# Revit family: Haworth_Tibas_Desk_Rectangular_EU_PRELIMINARY1
name_source: partatom
category: Furniture
units: mm (PartAtom-declared; Revit-internal decimal feet)

## family parameters
Always vertical = Yes
Cut with Voids When Loaded = No
OmniClass Number = 23.40.70.14.64.11
OmniClass Title = Office Furniture
Room Calculation Point = No
Shared = No
Work Plane-Based = No

## types (5) — shared parameters
80cm = No
Assembly Code = E2020200
Cable Tray Finish = Haworth _ Paint _ Metallic Silver
Description = Haworth - Tibas - Desk - Rectangular
Manufacturer = Haworth
Model = TILDXXXX
Product URL = https://www.haworth.com
Revision Number = 1
Size = Verify Final Dim.w/ Haworth
Trim Finish = Haworth _ Polymer _ Undecided
URL = https://www.haworth.com
Warranty = http://www.haworth.com
Worksurface Depth = 60, 70, 80, 90cm
Worksurface Width = 120, 140, 160, 180, 200cm

## per-type parameters (varying)
| type | 100cm | 120cm | 140cm | 160cm | 180cm | 60 Depth | 70 Depth | 80 Depth | 90 Depth | Accessory Kit | Actual Depth | Actual Height | Actual Width | Cable Tray Width | Epure Cable Outlet | Flip Top Cable Outlet | Horizontal Cable Tray Single | Horizontal Cable Tray Wire Single | Leg Height | No Accessory Kit | Return Extension | Round Cable Outlet | Structure | U Shape Cable Outlet |
| 120w | Yes | No | No | No | No | Yes | No | No | No | Yes | 60 cm | 84 cm | 120 cm | 70 cm | Yes | No | Yes | No | 80 cm | No | No | No | Yes | No |
| 140w | No | Yes | No | No | No | No | Yes | No | No | Yes | 70 cm | 84 cm | 140 cm | 90 cm | No | Yes | No | Yes | 80 cm | No | No | No | Yes | No |
| 160w | No | No | Yes | No | No | No | No | Yes | No | Yes | 80 cm | 74 cm | 160 cm | 110 cm | No | No | Yes | No | 71 cm | No | No | Yes | Yes | No |
| 180w | No | No | No | Yes | No | No | No | No | Yes | Yes | 90 cm | 84 cm | 180 cm | 130 cm | No | No | No | Yes | 80 cm | No | Yes | No | No | Yes |
| 200w | No | No | No | No | Yes | No | No | No | Yes | No | 90 cm | 84 cm | 200 cm | 150 cm | No | No | No | No | 80 cm | Yes | Yes | No | No | No |

## geometry (parser evidence)
native form markers: Sweep x35
no freeform markers — native parametric forms only
